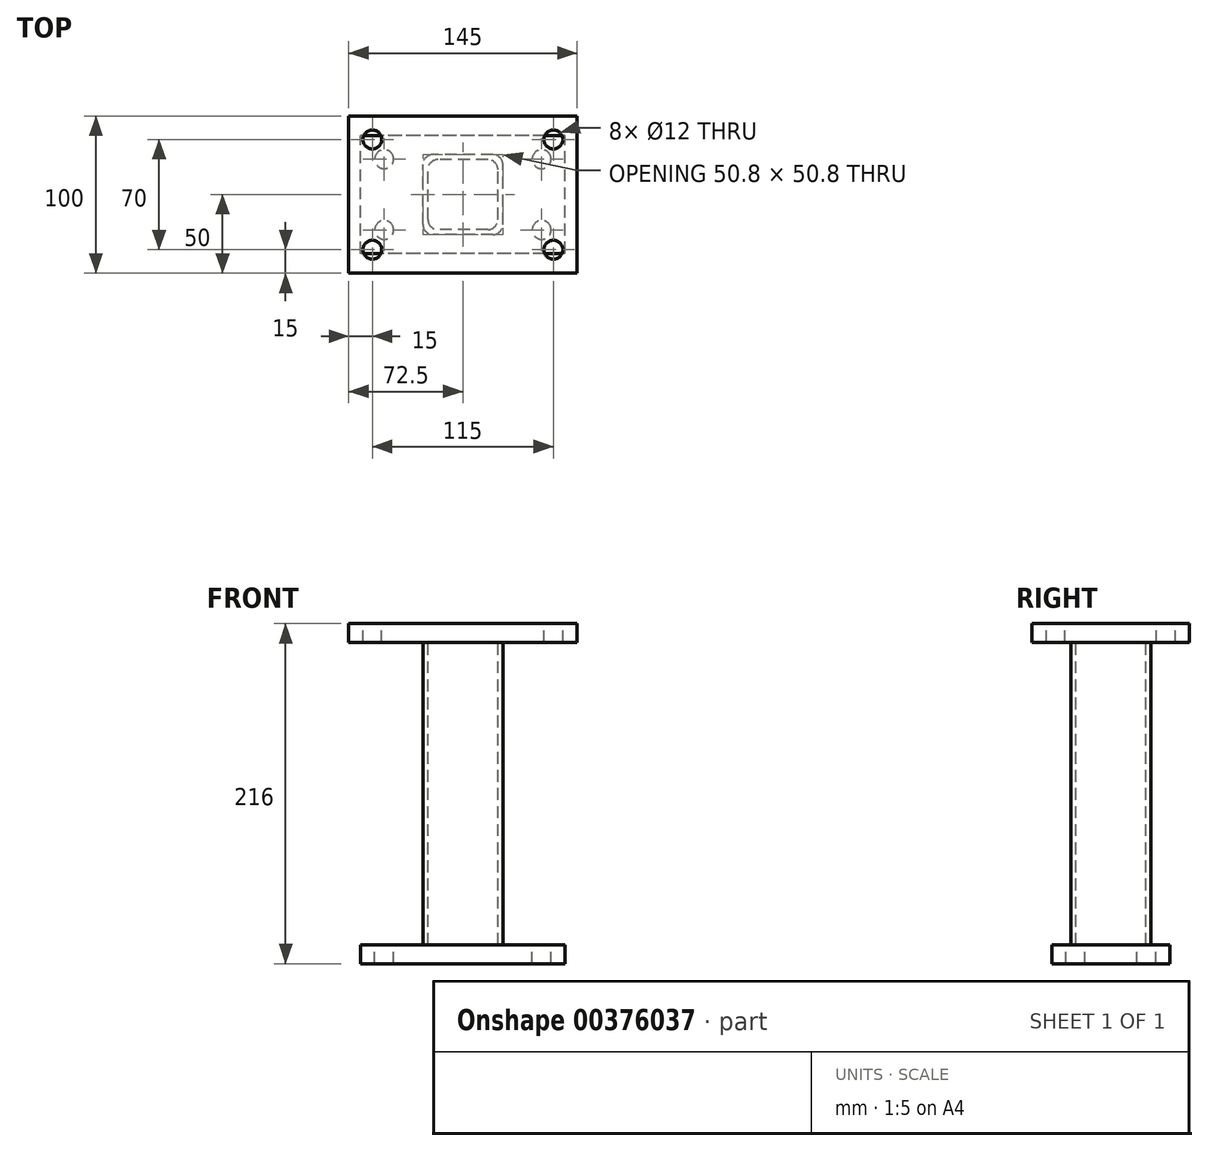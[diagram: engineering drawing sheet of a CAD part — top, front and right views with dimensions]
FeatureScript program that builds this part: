
annotation { "Feature Type Name" : "Feature", "Feature Type Description" : "" }
export const myFeature = defineFeature(function(context is Context, id is Id, definition is map)
    precondition{}
    {
        {
            var Q0;
            Q0=qCreatedBy(makeId("Top.planeOp"),FACE);
            var sketch = newSketch(context, id + "F0", { "sketchPlane" : qUnion([Q0])});
            skLineSegment(sketch, "E0.bottom", {"start": v(0, 0) * mm, "end": v(145, 0) * mm});
            skLineSegment(sketch, "E0.top", {"start": v(0, 100) * mm, "end": v(145, 100) * mm});
            skLineSegment(sketch, "E0.left", {"start": v(0, 0) * mm, "end": v(0, 100) * mm});
            skLineSegment(sketch, "E0.right", {"start": v(145, 0) * mm, "end": v(145, 100) * mm});
            skSolve(sketch);
        }
        {
            var Q0;
            Q0=makeQuery(id+"F0.imprint","IMPRINT",FACE,{"disambiguationData":[TD([[makeQuery(id+"F0.imprint","IMPRINT",EDGE,{"derivedFrom":sQuery(id+"F0.wireOp",EDGE,"E0.bottom")}),1.0]])]});
            extrude(context, id + "F1", {"entities" : qUnion([Q0]), "depth" : 12 * mm});
        }
        {
            var Q0;
            Q0=makeQuery(id+"F1.opExtrude","CAP_FACE",FACE,{"disambiguationData":[OSD([sQuery(id+"F0.wireOp",EDGE,"E0.bottom"),sQuery(id+"F0.wireOp",EDGE,"E0.top"),sQuery(id+"F0.wireOp",EDGE,"E0.left"),sQuery(id+"F0.wireOp",EDGE,"E0.right")])],"isStart":true});
            var sketch = newSketch(context, id + "F2", { "sketchPlane" : qUnion([Q0])});
            skLineSegment(sketch, "E1.bottom", {"start": v(91.55, -24.6) * mm, "end": v(53.45, -24.6) * mm});
            skLineSegment(sketch, "E1.top", {"start": v(91.55, -75.4) * mm, "end": v(53.45, -75.4) * mm});
            skLineSegment(sketch, "E1.left", {"start": v(97.9, -30.95) * mm, "end": v(97.9, -69.05) * mm});
            skLineSegment(sketch, "E1.right", {"start": v(47.1, -30.95) * mm, "end": v(47.1, -69.05) * mm});
            skPoint(sketch, "E1.middle", {"position": v(72.5, -50) * mm});
            skPoint(sketch, "E1.middle.positionSnap0", {"position": v(72.5, -100) * mm});
            skPoint(sketch, "E1.middle.positionSnap1", {"position": v(0, -50) * mm});
            skPoint(sketch, "E1.centerSnap0", {"position": v(72.5, -100) * mm});
            skPoint(sketch, "E1.centerSnap1", {"position": v(0, -50) * mm});
            skLineSegment(sketch, "E2.bottom", {"start": v(88.37, -27.77) * mm, "end": v(56.62, -27.77) * mm});
            skLineSegment(sketch, "E2.top", {"start": v(88.37, -72.22) * mm, "end": v(56.62, -72.22) * mm});
            skLineSegment(sketch, "E2.left", {"start": v(94.72, -34.12) * mm, "end": v(94.72, -65.87) * mm});
            skLineSegment(sketch, "E2.right", {"start": v(50.27, -34.12) * mm, "end": v(50.27, -65.87) * mm});
            skPoint(sketch, "E3.visualSharp", {"position": v(97.9, -24.6) * mm});
            skArc(sketch, "E3.filletArc", {"start": v(97.9, -30.95) * mm, "mid": v(96.04, -26.46) * mm, "end": v(91.55, -24.6) * mm});
            skPoint(sketch, "E4.visualSharp", {"position": v(97.9, -75.4) * mm});
            skArc(sketch, "E4.filletArc", {"start": v(91.55, -75.4) * mm, "mid": v(96.04, -73.54) * mm, "end": v(97.9, -69.05) * mm});
            skPoint(sketch, "E5.visualSharp", {"position": v(47.1, -75.4) * mm});
            skArc(sketch, "E5.filletArc", {"start": v(47.1, -69.05) * mm, "mid": v(48.96, -73.54) * mm, "end": v(53.45, -75.4) * mm});
            skPoint(sketch, "E6.visualSharp", {"position": v(47.1, -24.6) * mm});
            skArc(sketch, "E6.filletArc", {"start": v(53.45, -24.6) * mm, "mid": v(48.96, -26.46) * mm, "end": v(47.1, -30.95) * mm});
            skPoint(sketch, "E7.visualSharp", {"position": v(50.27, -27.77) * mm});
            skArc(sketch, "E7.filletArc", {"start": v(56.62, -27.77) * mm, "mid": v(52.13, -29.63) * mm, "end": v(50.27, -34.12) * mm});
            skPoint(sketch, "E8.visualSharp", {"position": v(50.27, -72.22) * mm});
            skArc(sketch, "E8.filletArc", {"start": v(50.27, -65.87) * mm, "mid": v(52.13, -70.37) * mm, "end": v(56.62, -72.23) * mm});
            skPoint(sketch, "E9.visualSharp", {"position": v(94.72, -72.22) * mm});
            skArc(sketch, "E9.filletArc", {"start": v(88.37, -72.22) * mm, "mid": v(92.87, -70.37) * mm, "end": v(94.72, -65.87) * mm});
            skPoint(sketch, "E10.visualSharp", {"position": v(94.72, -27.77) * mm});
            skArc(sketch, "E10.filletArc", {"start": v(94.72, -34.12) * mm, "mid": v(92.87, -29.63) * mm, "end": v(88.37, -27.78) * mm});
            skSolve(sketch);
        }
        {
            var Q0;
            Q0=makeQuery(id+"F2.imprint","IMPRINT",FACE,{"disambiguationData":[TD([[makeQuery(id+"F2.imprint","IMPRINT",EDGE,{"derivedFrom":sQuery(id+"F2.wireOp",EDGE,"E1.bottom")}),1.0]])]});
            extrude(context, id + "F3", {"entities" : qUnion([Q0]), "operationType" : NewBodyOperationType.ADD, "depth" : 192 * mm});
        }
        {
            var Q0;
            Q0=makeQuery(id+"F3.opExtrude","CAP_FACE",FACE,{"disambiguationData":[OSD([sQuery(id+"F2.wireOp",EDGE,"E1.bottom"),sQuery(id+"F2.wireOp",EDGE,"E1.top"),sQuery(id+"F2.wireOp",EDGE,"E1.left"),sQuery(id+"F2.wireOp",EDGE,"E1.right"),sQuery(id+"F2.wireOp",EDGE,"E2.bottom"),sQuery(id+"F2.wireOp",EDGE,"E2.top"),sQuery(id+"F2.wireOp",EDGE,"E2.left"),sQuery(id+"F2.wireOp",EDGE,"E2.right"),sQuery(id+"F2.wireOp",EDGE,"E3.filletArc"),sQuery(id+"F2.wireOp",EDGE,"E4.filletArc"),sQuery(id+"F2.wireOp",EDGE,"E5.filletArc"),sQuery(id+"F2.wireOp",EDGE,"E6.filletArc"),sQuery(id+"F2.wireOp",EDGE,"E7.filletArc"),sQuery(id+"F2.wireOp",EDGE,"E8.filletArc"),sQuery(id+"F2.wireOp",EDGE,"E9.filletArc"),sQuery(id+"F2.wireOp",EDGE,"E10.filletArc")])],"isStart":false});
            var sketch = newSketch(context, id + "F4", { "sketchPlane" : qUnion([Q0])});
            skLineSegment(sketch, "E11.bottom", {"start": v(137.5, -12.5) * mm, "end": v(7.5, -12.5) * mm});
            skLineSegment(sketch, "E11.top", {"start": v(137.5, -87.5) * mm, "end": v(7.5, -87.5) * mm});
            skLineSegment(sketch, "E11.left", {"start": v(137.5, -12.5) * mm, "end": v(137.5, -87.5) * mm});
            skLineSegment(sketch, "E11.right", {"start": v(7.5, -12.5) * mm, "end": v(7.5, -87.5) * mm});
            skPoint(sketch, "E11.middle", {"position": v(72.5, -50) * mm});
            skPoint(sketch, "E11.middle.positionSnap0", {"position": v(72.5, -27.77) * mm});
            skPoint(sketch, "E11.middle.positionSnap1", {"position": v(50.27, -50) * mm});
            skPoint(sketch, "E11.centerSnap0", {"position": v(72.5, -27.77) * mm});
            skPoint(sketch, "E11.centerSnap1", {"position": v(50.27, -50) * mm});
            skSolve(sketch);
        }
        {
            var Q0;
            Q0=makeQuery(id+"F4.imprint","IMPRINT",FACE,{"disambiguationData":[TD([[makeQuery(id+"F4.imprint","IMPRINT",EDGE,{"derivedFrom":sQuery(id+"F4.wireOp",EDGE,"E11.bottom")}),1.0]])]});
            var Q1;
            Q1=makeQuery(id+"F4.imprint","IMPRINT",FACE,{"disambiguationData":[TD([[makeQuery(id+"F4.imprint","IMPRINT",EDGE,{"derivedFrom":makeQuery(id+"F3.opExtrude","CAP_EDGE",EDGE,{"disambiguationData":[OSD([sQuery(id+"F2.wireOp",EDGE,"E1.bottom")])],"isStart":false})}),1.0]])]});
            var Q2;
            Q2=makeQuery(id+"F4.imprint","IMPRINT",FACE,{"disambiguationData":[TD([[makeQuery(id+"F4.imprint","IMPRINT",EDGE,{"derivedFrom":makeQuery(id+"F3.opExtrude","CAP_EDGE",EDGE,{"disambiguationData":[OSD([sQuery(id+"F2.wireOp",EDGE,"E2.bottom")])],"isStart":false})}),1.0]])]});
            extrude(context, id + "F5", {"entities" : qUnion([Q0, Q1, Q2]), "operationType" : NewBodyOperationType.ADD, "depth" : 12 * mm});
        }
        {
            var Q0;
            {var subQ0=sQuery(id+"F4.wireOp",EDGE,"E11.top");var subQ1=sQuery(id+"F4.wireOp",EDGE,"E11.bottom");var subQ2=sQuery(id+"F4.wireOp",EDGE,"E11.left");var subQ3=sQuery(id+"F4.wireOp",EDGE,"E11.right");Q0=makeQuery(id+"F5.boolean.opBoolean","SPLIT",FACE,{"disambiguationData":[TD([makeQuery(id+"F3.opExtrude","SWEPT_FACE",FACE,{"disambiguationData":[OSD([sQuery(id+"F2.wireOp",EDGE,"E1.bottom")])]})])],"derivedFrom":makeQuery(id+"F5.opExtrude","CAP_FACE",FACE,{"disambiguationData":[OSD([subQ1,subQ0,subQ2,subQ3])],"isStart":true})});}
            var sketch = newSketch(context, id + "F6", { "sketchPlane" : qUnion([Q0])});
            skLineSegment(sketch, "E12", {"start": v(137.5, 12.5) * mm, "end": v(122.5, 12.5) * mm, "construction": true});
            skLineSegment(sketch, "E13", {"start": v(122.5, 12.5) * mm, "end": v(122.5, 27.5) * mm, "construction": true});
            skLineSegment(sketch, "E14", {"start": v(72.5, 12.5) * mm, "end": v(72.5, 87.5) * mm, "construction": true});
            skLineSegment(sketch, "E15", {"start": v(7.5, 50) * mm, "end": v(137.5, 50) * mm, "construction": true});
            skLineSegment(sketch, "E16.MirrorCS", {"start": v(22.5, 12.5) * mm, "end": v(22.5, 27.5) * mm, "construction": true});
            skLineSegment(sketch, "E17.MirrorCS", {"start": v(122.5, 87.5) * mm, "end": v(122.5, 72.5) * mm, "construction": true});
            skLineSegment(sketch, "E18.MirrorCS", {"start": v(22.5, 87.5) * mm, "end": v(22.5, 72.5) * mm, "construction": true});
            skSolve(sketch);
        }
        {
            var Q0;
            Q0=sQuery(id+"F6.wireOp",VERTEX,"E17.MirrorCS.end");
            var Q1;
            Q1=sQuery(id+"F6.wireOp",VERTEX,"E13.end");
            var Q2;
            Q2=sQuery(id+"F6.wireOp",VERTEX,"E16.MirrorCS.end");
            var Q3;
            Q3=sQuery(id+"F6.wireOp",VERTEX,"E18.MirrorCS.end");
            var Q4;
            Q4=makeQuery(id+"F1.opExtrude","SWEPT_BODY",BODY,{"disambiguationData":[OSD([sQuery(id+"F0.wireOp",EDGE,"E0.bottom"),sQuery(id+"F0.wireOp",EDGE,"E0.top"),sQuery(id+"F0.wireOp",EDGE,"E0.left"),sQuery(id+"F0.wireOp",EDGE,"E0.right")])]});
            hole(context, id + "F7", {"style" : HoleStyle.SIMPLE, "endStyle" : HoleEndStyle.BLIND, "holeDiameter" : 12 * mm, "holeDepth" : 12 * mm, "isTappedThrough" : true, "tappedDepth" : 12 * mm, "tapClearance" : 3, "locations" : qUnion([Q0, Q1, Q2, Q3]), "scope" : qUnion([Q4])});
        }
        {
            var Q0;
            Q0=makeQuery(id+"F1.opExtrude","CAP_FACE",FACE,{"disambiguationData":[OSD([sQuery(id+"F0.wireOp",EDGE,"E0.bottom"),sQuery(id+"F0.wireOp",EDGE,"E0.top"),sQuery(id+"F0.wireOp",EDGE,"E0.left"),sQuery(id+"F0.wireOp",EDGE,"E0.right")])],"isStart":false});
            var sketch = newSketch(context, id + "F8", { "sketchPlane" : qUnion([Q0])});
            skLineSegment(sketch, "E19", {"start": v(145, 0) * mm, "end": v(130, 0) * mm, "construction": true});
            skLineSegment(sketch, "E20", {"start": v(130, 0) * mm, "end": v(130, 15) * mm, "construction": true});
            skLineSegment(sketch, "E21", {"start": v(0, 100) * mm, "end": v(0, 85) * mm, "construction": true});
            skLineSegment(sketch, "E22", {"start": v(0, 85) * mm, "end": v(15, 85) * mm, "construction": true});
            skLineSegment(sketch, "E23", {"start": v(0, 0) * mm, "end": v(15, 0) * mm, "construction": true});
            skLineSegment(sketch, "E24", {"start": v(15, 0) * mm, "end": v(15, 15) * mm, "construction": true});
            skLineSegment(sketch, "E25", {"start": v(145, 100) * mm, "end": v(130, 100) * mm, "construction": true});
            skLineSegment(sketch, "E26", {"start": v(130, 100) * mm, "end": v(130, 85) * mm, "construction": true});
            skSolve(sketch);
        }
        {
            var Q0;
            Q0=sQuery(id+"F8.wireOp",VERTEX,"E22.end");
            var Q1;
            Q1=sQuery(id+"F8.wireOp",VERTEX,"E26.end");
            var Q2;
            Q2=sQuery(id+"F8.wireOp",VERTEX,"E20.end");
            var Q3;
            Q3=sQuery(id+"F8.wireOp",VERTEX,"E24.end");
            var Q4;
            Q4=makeQuery(id+"F1.opExtrude","SWEPT_BODY",BODY,{"disambiguationData":[OSD([sQuery(id+"F0.wireOp",EDGE,"E0.bottom"),sQuery(id+"F0.wireOp",EDGE,"E0.top"),sQuery(id+"F0.wireOp",EDGE,"E0.left"),sQuery(id+"F0.wireOp",EDGE,"E0.right")])]});
            hole(context, id + "F9", {"style" : HoleStyle.SIMPLE, "endStyle" : HoleEndStyle.BLIND, "holeDiameter" : 12 * mm, "holeDepth" : 12 * mm, "isTappedThrough" : true, "tappedDepth" : 12 * mm, "tapClearance" : 3, "locations" : qUnion([Q0, Q1, Q2, Q3]), "scope" : qUnion([Q4])});
        }
    });
